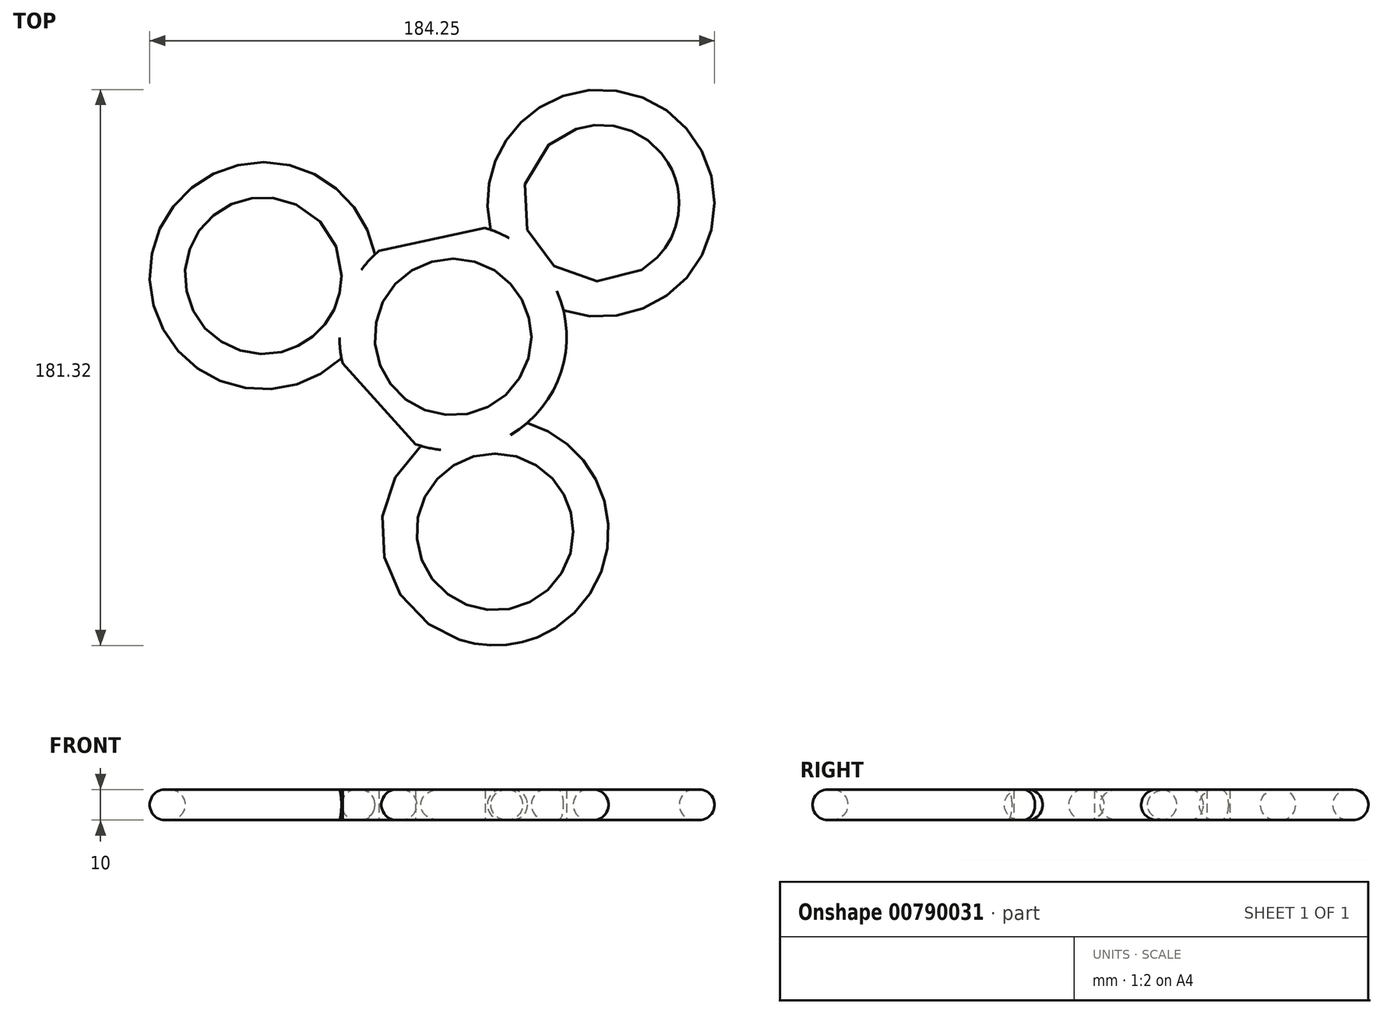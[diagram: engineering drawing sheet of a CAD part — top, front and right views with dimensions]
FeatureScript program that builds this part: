
annotation { "Feature Type Name" : "Feature", "Feature Type Description" : "" }
export const myFeature = defineFeature(function(context is Context, id is Id, definition is map)
    precondition{}
    {
        {
            var Q0;
            Q0=qCreatedBy(makeId("Top.planeOp"),FACE);
            var sketch = newSketch(context, id + "F0", { "sketchPlane" : qUnion([Q0])});
            skCircle(sketch, "E0", {"center": v(0, 0) * mm, "radius": 37.05 * mm});
            skCircle(sketch, "E1", {"center": v(0, 0) * mm, "radius": 25.55 * mm});
            skCircle(sketch, "E2.cCircle", {"center": v(0, 0) * mm, "radius": 65.04 * mm, "construction": true});
            skLineSegment(sketch, "E2.0", {"start": v(-61.9, 19.96) * mm, "end": v(48.24, 43.63) * mm});
            skLineSegment(sketch, "E2.1", {"start": v(48.24, 43.63) * mm, "end": v(13.67, -63.59) * mm});
            skLineSegment(sketch, "E2.2", {"start": v(13.67, -63.59) * mm, "end": v(-61.9, 19.96) * mm});
            skCircle(sketch, "E3", {"center": v(-61.9, 19.96) * mm, "radius": 37.05 * mm});
            skCircle(sketch, "E4", {"center": v(-61.9, 19.96) * mm, "radius": 25.55 * mm});
            skCircle(sketch, "E5", {"center": v(13.67, -63.59) * mm, "radius": 37.05 * mm});
            skCircle(sketch, "E6", {"center": v(13.67, -63.59) * mm, "radius": 25.55 * mm});
            skCircle(sketch, "E7", {"center": v(48.24, 43.63) * mm, "radius": 37.05 * mm});
            skCircle(sketch, "E8", {"center": v(48.24, 43.63) * mm, "radius": 25.55 * mm});
            skSolve(sketch);
        }
        {
            var Q0;
            {var subQ0=sQuery(id+"F0.wireOp",EDGE,"E3");var subQ1=sQuery(id+"F0.wireOp",EDGE,"E2.0");var subQ2=makeQuery(id+"F0.imprint","INTERSECT",VERTEX,{"derivedFrom":[subQ1,subQ0]});Q0=makeQuery(id+"F0.imprint","IMPRINT",FACE,{"disambiguationData":[TD([[makeQuery(id+"F0.imprint","IMPRINT",EDGE,{"disambiguationData":[TD([[subQ2,1.0]])],"derivedFrom":subQ1}),1.0]])]});}
            var Q1;
            Q1=makeQuery(id+"F0.imprint","IMPRINT",FACE,{"disambiguationData":[TD([[makeQuery(id+"F0.imprint","IMPRINT",EDGE,{"derivedFrom":sQuery(id+"F0.wireOp",EDGE,"E1")}),-1.0]])]});
            var Q2;
            {var subQ0=sQuery(id+"F0.wireOp",EDGE,"E7");var subQ1=sQuery(id+"F0.wireOp",EDGE,"E2.0");var subQ2=makeQuery(id+"F0.imprint","INTERSECT",VERTEX,{"derivedFrom":[subQ1,subQ0]});Q2=makeQuery(id+"F0.imprint","IMPRINT",FACE,{"disambiguationData":[TD([[makeQuery(id+"F0.imprint","IMPRINT",EDGE,{"disambiguationData":[TD([[subQ2,-1.0]])],"derivedFrom":subQ1}),1.0]])]});}
            var Q3;
            {var subQ0=sQuery(id+"F0.wireOp",EDGE,"E5");var subQ1=sQuery(id+"F0.wireOp",EDGE,"E2.1");var subQ2=makeQuery(id+"F0.imprint","INTERSECT",VERTEX,{"derivedFrom":[subQ1,subQ0]});Q3=makeQuery(id+"F0.imprint","IMPRINT",FACE,{"disambiguationData":[TD([[makeQuery(id+"F0.imprint","IMPRINT",EDGE,{"disambiguationData":[TD([[subQ2,-1.0]])],"derivedFrom":subQ1}),1.0]])]});}
            var Q4;
            {var subQ0=sQuery(id+"F0.wireOp",EDGE,"E3");var subQ1=sQuery(id+"F0.wireOp",EDGE,"E0");var subQ2=makeQuery(id+"F0.imprint","INTERSECT",VERTEX,{"disambiguationData":[OD(0.0)],"derivedFrom":[subQ1,subQ0]});Q4=makeQuery(id+"F0.imprint","IMPRINT",FACE,{"disambiguationData":[TD([[makeQuery(id+"F0.imprint","IMPRINT",EDGE,{"disambiguationData":[TD([[subQ2,-1.0]])],"derivedFrom":subQ1}),1.0]])]});}
            var Q5;
            {var subQ0=sQuery(id+"F0.wireOp",EDGE,"E3");var subQ7=sQuery(id+"F0.wireOp",EDGE,"E0");var subQ8=makeQuery(id+"F0.imprint","INTERSECT",VERTEX,{"disambiguationData":[OD(0.0)],"derivedFrom":[subQ7,subQ0]});Q5=makeQuery(id+"F0.imprint","IMPRINT",FACE,{"disambiguationData":[TD([[makeQuery(id+"F0.imprint","IMPRINT",EDGE,{"disambiguationData":[TD([[subQ8,-1.0]])],"derivedFrom":subQ7}),-1.0]])]});}
            var Q6;
            {var subQ0=sQuery(id+"F0.wireOp",EDGE,"E7");var subQ1=sQuery(id+"F0.wireOp",EDGE,"E0");var subQ2=makeQuery(id+"F0.imprint","INTERSECT",VERTEX,{"disambiguationData":[OD(0.0)],"derivedFrom":[subQ1,subQ0]});Q6=makeQuery(id+"F0.imprint","IMPRINT",FACE,{"disambiguationData":[TD([[makeQuery(id+"F0.imprint","IMPRINT",EDGE,{"disambiguationData":[TD([[subQ2,-1.0]])],"derivedFrom":subQ1}),1.0]])]});}
            var Q7;
            {var subQ0=sQuery(id+"F0.wireOp",EDGE,"E7");var subQ5=sQuery(id+"F0.wireOp",EDGE,"E0");var subQ10=makeQuery(id+"F0.imprint","INTERSECT",VERTEX,{"disambiguationData":[OD(0.0)],"derivedFrom":[subQ5,subQ0]});Q7=makeQuery(id+"F0.imprint","IMPRINT",FACE,{"disambiguationData":[TD([[makeQuery(id+"F0.imprint","IMPRINT",EDGE,{"disambiguationData":[TD([[subQ10,-1.0]])],"derivedFrom":subQ5}),-1.0]])]});}
            var Q8;
            {var subQ0=sQuery(id+"F0.wireOp",EDGE,"E5");var subQ1=sQuery(id+"F0.wireOp",EDGE,"E0");var subQ2=makeQuery(id+"F0.imprint","INTERSECT",VERTEX,{"disambiguationData":[OD(0.0)],"derivedFrom":[subQ1,subQ0]});Q8=makeQuery(id+"F0.imprint","IMPRINT",FACE,{"disambiguationData":[TD([[makeQuery(id+"F0.imprint","IMPRINT",EDGE,{"disambiguationData":[TD([[subQ2,-1.0]])],"derivedFrom":subQ1}),1.0]])]});}
            var Q9;
            {var subQ0=sQuery(id+"F0.wireOp",EDGE,"E5");var subQ7=sQuery(id+"F0.wireOp",EDGE,"E0");var subQ10=makeQuery(id+"F0.imprint","INTERSECT",VERTEX,{"disambiguationData":[OD(0.0)],"derivedFrom":[subQ7,subQ0]});Q9=makeQuery(id+"F0.imprint","IMPRINT",FACE,{"disambiguationData":[TD([[makeQuery(id+"F0.imprint","IMPRINT",EDGE,{"disambiguationData":[TD([[subQ10,-1.0]])],"derivedFrom":subQ7}),-1.0]])]});}
            var Q10;
            {var subQ0=sQuery(id+"F0.wireOp",EDGE,"E2.1");var subQ1=sQuery(id+"F0.wireOp",EDGE,"E0");var subQ2=makeQuery(id+"F0.imprint","INTERSECT",VERTEX,{"disambiguationData":[OD(0.0)],"derivedFrom":[subQ1,subQ0]});Q10=makeQuery(id+"F0.imprint","IMPRINT",FACE,{"disambiguationData":[TD([[makeQuery(id+"F0.imprint","IMPRINT",EDGE,{"disambiguationData":[TD([[subQ2,1.0]])],"derivedFrom":subQ1}),1.0]])]});}
            var Q11;
            {var subQ0=sQuery(id+"F0.wireOp",EDGE,"E2.0");var subQ1=sQuery(id+"F0.wireOp",EDGE,"E0");var subQ2=makeQuery(id+"F0.imprint","INTERSECT",VERTEX,{"disambiguationData":[OD(0.0)],"derivedFrom":[subQ1,subQ0]});Q11=makeQuery(id+"F0.imprint","IMPRINT",FACE,{"disambiguationData":[TD([[makeQuery(id+"F0.imprint","IMPRINT",EDGE,{"disambiguationData":[TD([[subQ2,-1.0]])],"derivedFrom":subQ1}),1.0]])]});}
            var Q12;
            {var subQ0=sQuery(id+"F0.wireOp",EDGE,"E2.2");var subQ1=sQuery(id+"F0.wireOp",EDGE,"E0");var subQ2=makeQuery(id+"F0.imprint","INTERSECT",VERTEX,{"disambiguationData":[OD(0.0)],"derivedFrom":[subQ1,subQ0]});Q12=makeQuery(id+"F0.imprint","IMPRINT",FACE,{"disambiguationData":[TD([[makeQuery(id+"F0.imprint","IMPRINT",EDGE,{"disambiguationData":[TD([[subQ2,-1.0]])],"derivedFrom":subQ1}),1.0]])]});}
            extrude(context, id + "F1", {"entities" : qUnion([Q0, Q1, Q2, Q3, Q4, Q5, Q6, Q7, Q8, Q9, Q10, Q11, Q12]), "depth" : 10 * mm, "offsetDistance" : 25 * mm});
        }
        {
            var Q0;
            Q0=makeQuery(id+"F1.opExtrude","CAP_EDGE",EDGE,{"disambiguationData":[OSD([sQuery(id+"F0.wireOp",EDGE,"E3")])],"isStart":false});
            var Q1;
            Q1=makeQuery(id+"F1.opExtrude","CAP_EDGE",EDGE,{"disambiguationData":[OSD([sQuery(id+"F0.wireOp",EDGE,"E7")])],"isStart":false});
            var Q2;
            Q2=makeQuery(id+"F1.opExtrude","CAP_EDGE",EDGE,{"disambiguationData":[OSD([sQuery(id+"F0.wireOp",EDGE,"E5")])],"isStart":false});
            var Q3;
            Q3=makeQuery(id+"F1.opExtrude","CAP_EDGE",EDGE,{"disambiguationData":[OSD([sQuery(id+"F0.wireOp",EDGE,"E4")])],"isStart":false});
            var Q4;
            Q4=makeQuery(id+"F1.opExtrude","CAP_EDGE",EDGE,{"disambiguationData":[OSD([sQuery(id+"F0.wireOp",EDGE,"E8")])],"isStart":false});
            var Q5;
            Q5=makeQuery(id+"F1.opExtrude","CAP_EDGE",EDGE,{"disambiguationData":[OSD([sQuery(id+"F0.wireOp",EDGE,"E6")])],"isStart":false});
            var Q6;
            Q6=makeQuery(id+"F1.opExtrude","CAP_EDGE",EDGE,{"disambiguationData":[OSD([sQuery(id+"F0.wireOp",EDGE,"E1")])],"isStart":false});
            var Q7;
            Q7=makeQuery(id+"F1.opExtrude","CAP_EDGE",EDGE,{"disambiguationData":[OSD([sQuery(id+"F0.wireOp",EDGE,"E8")])],"isStart":true});
            var Q8;
            Q8=makeQuery(id+"F1.opExtrude","CAP_EDGE",EDGE,{"disambiguationData":[OSD([sQuery(id+"F0.wireOp",EDGE,"E7")])],"isStart":true});
            var Q9;
            Q9=makeQuery(id+"F1.opExtrude","CAP_EDGE",EDGE,{"disambiguationData":[OSD([sQuery(id+"F0.wireOp",EDGE,"E1")])],"isStart":true});
            var Q10;
            Q10=makeQuery(id+"F1.opExtrude","CAP_EDGE",EDGE,{"disambiguationData":[OSD([sQuery(id+"F0.wireOp",EDGE,"E4")])],"isStart":true});
            var Q11;
            Q11=makeQuery(id+"F1.opExtrude","CAP_EDGE",EDGE,{"disambiguationData":[OSD([sQuery(id+"F0.wireOp",EDGE,"E3")])],"isStart":true});
            var Q12;
            Q12=makeQuery(id+"F1.opExtrude","CAP_EDGE",EDGE,{"disambiguationData":[OSD([sQuery(id+"F0.wireOp",EDGE,"E6")])],"isStart":true});
            var Q13;
            Q13=makeQuery(id+"F1.opExtrude","CAP_EDGE",EDGE,{"disambiguationData":[OSD([sQuery(id+"F0.wireOp",EDGE,"E5")])],"isStart":true});
            fillet(context, id + "F2", {"entities" : qUnion([Q0, Q1, Q2, Q3, Q4, Q5, Q6, Q7, Q8, Q9, Q10, Q11, Q12, Q13]), "radius" : 5 * mm, "tangentPropagation" : true, "allowEdgeOverflow" : false});
        }
    });
